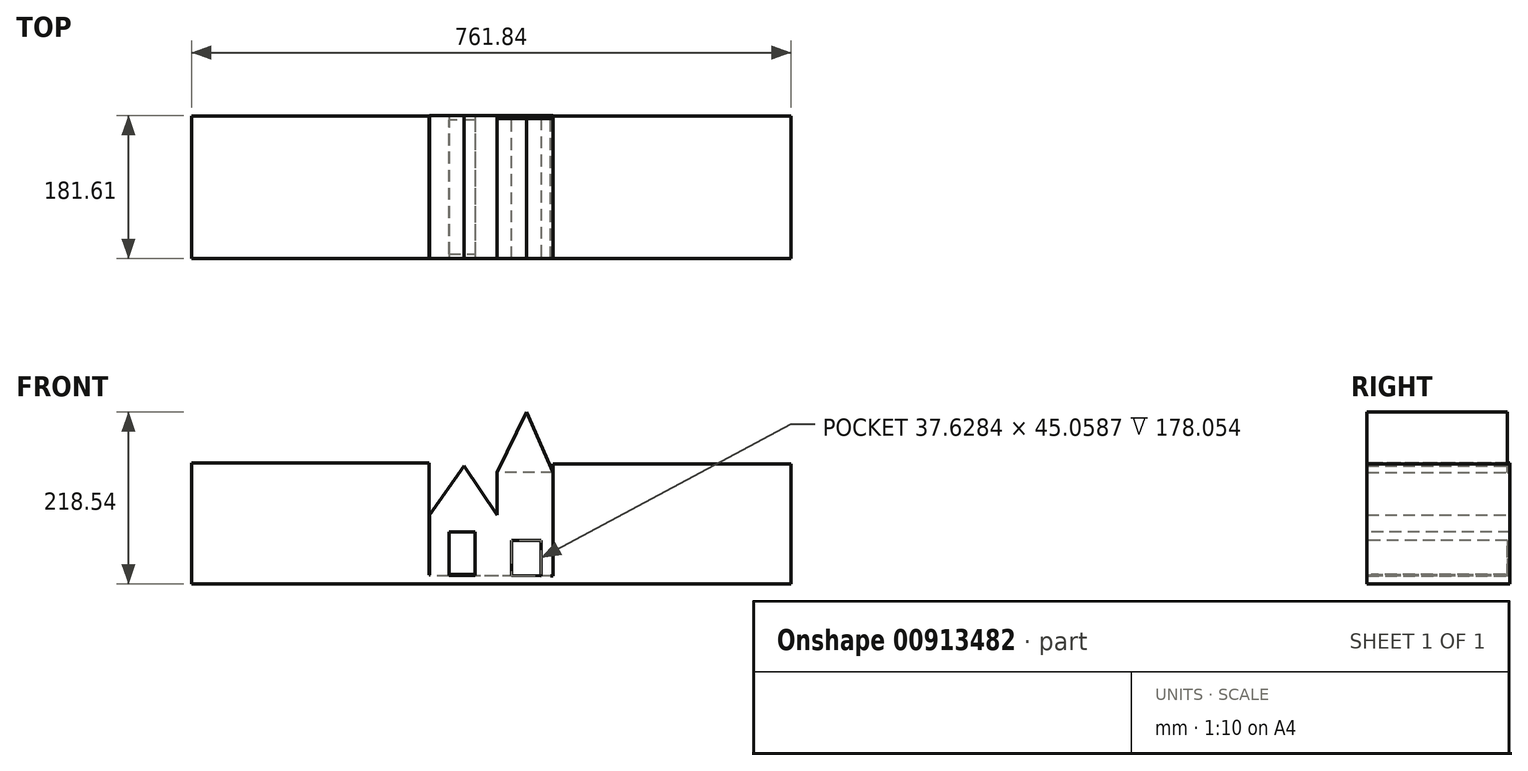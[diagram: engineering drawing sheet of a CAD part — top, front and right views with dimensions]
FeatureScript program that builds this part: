
annotation { "Feature Type Name" : "Feature", "Feature Type Description" : "" }
export const myFeature = defineFeature(function(context is Context, id is Id, definition is map)
    precondition{}
    {
        {
            var Q0;
            Q0=qCreatedBy(makeId("Front.planeOp"),FACE);
            var sketch = newSketch(context, id + "F0", { "sketchPlane" : qUnion([Q0])});
            skLineSegment(sketch, "E0", {"start": v(42.3, -77.57) * mm, "end": v(42.3, 0) * mm});
            skLineSegment(sketch, "E1", {"start": v(42.3, 0) * mm, "end": v(0, 62.2) * mm});
            skLineSegment(sketch, "E2", {"start": v(42.3, -77.57) * mm, "end": v(-43.65, -77.57) * mm});
            skLineSegment(sketch, "E3", {"start": v(0, 62.2) * mm, "end": v(-43.65, 0) * mm});
            skLineSegment(sketch, "E4", {"start": v(-43.65, 0) * mm, "end": v(-43.65, -77.57) * mm});
            skSolve(sketch);
        }
        {
            var Q0;
            Q0=makeQuery(id+"F0.imprint","IMPRINT",FACE,{"disambiguationData":[TD([[makeQuery(id+"F0.imprint","IMPRINT",EDGE,{"derivedFrom":sQuery(id+"F0.wireOp",EDGE,"E0")}),1.0]])]});
            extrude(context, id + "F1", {"entities" : qUnion([Q0]), "depth" : 25.4 * mm, "offsetDistance" : 25.4 * mm});
        }
        {
            var Q0;
            Q0=makeQuery(id+"F1.opExtrude","CAP_FACE",FACE,{"disambiguationData":[OSD([sQuery(id+"F0.wireOp",EDGE,"E0"),sQuery(id+"F0.wireOp",EDGE,"E1"),sQuery(id+"F0.wireOp",EDGE,"E2"),sQuery(id+"F0.wireOp",EDGE,"E3"),sQuery(id+"F0.wireOp",EDGE,"E4")])],"isStart":false});
            extrude(context, id + "F2", {"entities" : qUnion([Q0]), "operationType" : NewBodyOperationType.ADD, "depth" : 105.4 * mm, "offsetDistance" : 25.4 * mm});
        }
        {
            var Q0;
            Q0=makeQuery(id+"F2.opExtrude","CAP_FACE",FACE,{"disambiguationData":[OSD([sQuery(id+"F0.wireOp",EDGE,"E0"),sQuery(id+"F0.wireOp",EDGE,"E1"),sQuery(id+"F0.wireOp",EDGE,"E2"),sQuery(id+"F0.wireOp",EDGE,"E3"),sQuery(id+"F0.wireOp",EDGE,"E4")])],"isStart":false});
            var sketch = newSketch(context, id + "F3", { "sketchPlane" : qUnion([Q0])});
            skSolve(sketch);
        }
        {
            var Q0;
            Q0=makeQuery(id+"F3.imprint","IMPRINT",FACE,{"disambiguationData":[TD([[makeQuery(id+"F3.imprint","IMPRINT",EDGE,{"derivedFrom":makeQuery(id+"F2.opExtrude","CAP_EDGE",EDGE,{"disambiguationData":[OSD([sQuery(id+"F0.wireOp",EDGE,"E0")])],"isStart":false})}),1.0]])]});
            extrude(context, id + "F4", {"entities" : qUnion([Q0]), "operationType" : NewBodyOperationType.ADD, "depth" : 25.4 * mm, "offsetDistance" : 25.4 * mm});
        }
        {
            var Q0;
            Q0=makeQuery(id+"F4.opExtrude","CAP_FACE",FACE,{"disambiguationData":[OSD([sQuery(id+"F0.wireOp",EDGE,"E0"),sQuery(id+"F0.wireOp",EDGE,"E1"),sQuery(id+"F0.wireOp",EDGE,"E2"),sQuery(id+"F0.wireOp",EDGE,"E3"),sQuery(id+"F0.wireOp",EDGE,"E4")])],"isStart":false});
            var sketch = newSketch(context, id + "F5", { "sketchPlane" : qUnion([Q0])});
            skLineSegment(sketch, "E5", {"start": v(13.7, -77.57) * mm, "end": v(13.7, -34.13) * mm});
            skLineSegment(sketch, "E6", {"start": v(13.7, -77.57) * mm, "end": v(-17.83, -77.57) * mm});
            skLineSegment(sketch, "E7", {"start": v(-17.83, -78.03) * mm, "end": v(-17.83, -37.08) * mm});
            skLineSegment(sketch, "E8", {"start": v(-16.65, -37.08) * mm, "end": v(13.7, -37.08) * mm});
            skSolve(sketch);
        }
        {
            var Q0;
            {var subQ1=sQuery(id+"F5.wireOp",EDGE,"E6");Q0=makeQuery(id+"F5.imprint","IMPRINT",FACE,{"disambiguationData":[TD([[makeQuery(id+"F5.imprint","IMPRINT",EDGE,{"derivedFrom":subQ1}),-1.0]])]});}
            var sketch = newSketch(context, id + "F6", { "sketchPlane" : qUnion([Q0])});
            skLineSegment(sketch, "E9", {"start": v(-16.94, -78.91) * mm, "end": v(-16.94, -35.6) * mm});
            skLineSegment(sketch, "E10", {"start": v(-19.3, -35.6) * mm, "end": v(14, -35.6) * mm});
            skLineSegment(sketch, "E11", {"start": v(14, -35.01) * mm, "end": v(14, -78.33) * mm});
            skLineSegment(sketch, "E12", {"start": v(14, -78.33) * mm, "end": v(-16.94, -78.91) * mm});
            skSolve(sketch);
        }
        {
            var Q0;
            {var subQ1=sQuery(id+"F6.wireOp",EDGE,"E10");var subQ9=sQuery(id+"F6.wireOp",EDGE,"E9");var subQ11=makeQuery(id+"F6.imprint","INTERSECT",VERTEX,{"derivedFrom":[subQ9,subQ1]});Q0=makeQuery(id+"F6.imprint","IMPRINT",FACE,{"disambiguationData":[TD([[makeQuery(id+"F6.imprint","IMPRINT",EDGE,{"disambiguationData":[TD([[subQ11,1.0]])],"derivedFrom":subQ9}),-1.0]])]});}
            extrude(context, id + "F7", {"entities" : qUnion([Q0]), "operationType" : NewBodyOperationType.ADD, "oppositeDirection" : true, "depth" : 34.54 * mm, "offsetDistance" : 25.4 * mm});
        }
        {
            var Q0;
            {var subQ1=sQuery(id+"F5.wireOp",EDGE,"E6");Q0=makeQuery(id+"F5.imprint","IMPRINT",FACE,{"disambiguationData":[TD([[makeQuery(id+"F5.imprint","IMPRINT",EDGE,{"derivedFrom":subQ1}),-1.0]])]});}
            extrude(context, id + "F8", {"entities" : qUnion([Q0]), "operationType" : NewBodyOperationType.ADD, "depth" : 25.4 * mm, "offsetDistance" : 25.4 * mm});
        }
        {
            var Q0;
            Q0=makeQuery(id+"F8.opExtrude","CAP_FACE",FACE,{"disambiguationData":[OSD([sQuery(id+"F0.wireOp",EDGE,"E0"),sQuery(id+"F0.wireOp",EDGE,"E1"),sQuery(id+"F0.wireOp",EDGE,"E2"),sQuery(id+"F0.wireOp",EDGE,"E3"),sQuery(id+"F0.wireOp",EDGE,"E4"),sQuery(id+"F5.wireOp",EDGE,"E6")])],"isStart":false});
            var sketch = newSketch(context, id + "F9", { "sketchPlane" : qUnion([Q0])});
            skLineSegment(sketch, "E13", {"start": v(-19, -77.57) * mm, "end": v(-19, -22.05) * mm});
            skLineSegment(sketch, "E14", {"start": v(-19, -22.05) * mm, "end": v(14.3, -22.05) * mm});
            skLineSegment(sketch, "E15", {"start": v(14.3, -22.05) * mm, "end": v(14.3, -77.57) * mm});
            skLineSegment(sketch, "E16", {"start": v(14.3, -77.57) * mm, "end": v(-19, -77.57) * mm});
            skSolve(sketch);
        }
        {
            var Q0;
            Q0=makeQuery(id+"F9.imprint","IMPRINT",FACE,{"disambiguationData":[TD([[makeQuery(id+"F9.imprint","IMPRINT",EDGE,{"derivedFrom":sQuery(id+"F9.wireOp",EDGE,"E13")}),-1.0]])]});
            extrude(context, id + "F10", {"entities" : qUnion([Q0]), "operationType" : NewBodyOperationType.ADD, "depth" : 25.4 * mm, "offsetDistance" : 25.4 * mm});
        }
        {
            var Q0;
            Q0=makeQuery(id+"F10.opExtrude","CAP_FACE",FACE,{"disambiguationData":[OSD([sQuery(id+"F9.wireOp",EDGE,"E13"),sQuery(id+"F9.wireOp",EDGE,"E14"),sQuery(id+"F9.wireOp",EDGE,"E15"),sQuery(id+"F9.wireOp",EDGE,"E16")])],"isStart":false});
            extrude(context, id + "F11", {"entities" : qUnion([Q0]), "operationType" : NewBodyOperationType.REMOVE, "oppositeDirection" : true, "depth" : 249.68 * mm, "offsetDistance" : 25.4 * mm});
        }
        {
            var Q0;
            {var subQ0=sQuery(id+"F0.wireOp",EDGE,"E4");var subQ2=sQuery(id+"F0.wireOp",EDGE,"E2");var subQ5=sQuery(id+"F5.wireOp",EDGE,"E6");Q0=makeQuery(id+"F11.boolean.opBoolean","SPLIT",FACE,{"disambiguationData":[TD([makeQuery(id+"F1.opExtrude","SWEPT_FACE",FACE,{"disambiguationData":[OSD([subQ0])]})])],"derivedFrom":makeQuery(id+"F10.boolean.opBoolean","MERGE",FACE,{"derivedFrom":[makeQuery(id+"F8.boolean.opBoolean","MERGE",FACE,{"derivedFrom":[makeQuery(id+"F4.boolean.opBoolean","MERGE",FACE,{"derivedFrom":[makeQuery(id+"F2.boolean.opBoolean","MERGE",FACE,{"derivedFrom":[makeQuery(id+"F1.opExtrude","SWEPT_FACE",FACE,{"disambiguationData":[OSD([subQ2])]}),makeQuery(id+"F2.opExtrude","SWEPT_FACE",FACE,{"disambiguationData":[OSD([subQ2])]})]}),makeQuery(id+"F4.opExtrude","SWEPT_FACE",FACE,{"disambiguationData":[OSD([subQ2])]})]}),makeQuery(id+"F8.opExtrude","SWEPT_FACE",FACE,{"disambiguationData":[OSD([subQ2,subQ5])]})]}),makeQuery(id+"F10.opExtrude","SWEPT_FACE",FACE,{"disambiguationData":[OSD([sQuery(id+"F9.wireOp",EDGE,"E16")])]})]})});}
            var sketch = newSketch(context, id + "F12", { "sketchPlane" : qUnion([Q0])});
            skLineSegment(sketch, "E17", {"start": v(-38.28, 175.95) * mm, "end": v(-38.28, 6.02) * mm});
            skLineSegment(sketch, "E18", {"start": v(-38.28, 6.02) * mm, "end": v(34.83, 6.02) * mm});
            skLineSegment(sketch, "E19", {"start": v(34.83, 6.02) * mm, "end": v(34.83, 175.95) * mm});
            skLineSegment(sketch, "E20", {"start": v(34.83, 175.95) * mm, "end": v(-38.28, 175.95) * mm});
            skSolve(sketch);
        }
        {
            var Q0;
            {var subQ0=sQuery(id+"F12.wireOp",EDGE,"E19");Q0=makeQuery(id+"F12.imprint","IMPRINT",FACE,{"disambiguationData":[TD([[makeQuery(id+"F12.imprint","IMPRINT",EDGE,{"derivedFrom":subQ0}),1.0]])]});}
            var Q1;
            {var subQ0=sQuery(id+"F12.wireOp",EDGE,"E17");Q1=makeQuery(id+"F12.imprint","IMPRINT",FACE,{"disambiguationData":[TD([[makeQuery(id+"F12.imprint","IMPRINT",EDGE,{"derivedFrom":subQ0}),1.0]])]});}
            extrude(context, id + "F13", {"entities" : qUnion([Q0, Q1]), "operationType" : NewBodyOperationType.ADD, "oppositeDirection" : true, "depth" : 1.52 * mm, "offsetDistance" : 25.4 * mm});
        }
        {
            var Q0;
            {var subQ0=sQuery(id+"F0.wireOp",EDGE,"E0");Q0=makeQuery(id+"F8.boolean.opBoolean","MERGE",FACE,{"derivedFrom":[makeQuery(id+"F4.boolean.opBoolean","MERGE",FACE,{"derivedFrom":[makeQuery(id+"F2.boolean.opBoolean","MERGE",FACE,{"derivedFrom":[makeQuery(id+"F1.opExtrude","SWEPT_FACE",FACE,{"disambiguationData":[OSD([subQ0])]}),makeQuery(id+"F2.opExtrude","SWEPT_FACE",FACE,{"disambiguationData":[OSD([subQ0])]})]}),makeQuery(id+"F4.opExtrude","SWEPT_FACE",FACE,{"disambiguationData":[OSD([subQ0])]})]}),makeQuery(id+"F8.opExtrude","SWEPT_FACE",FACE,{"disambiguationData":[OSD([subQ0])]})]});}
            extrude(context, id + "F14", {"entities" : qUnion([Q0]), "operationType" : NewBodyOperationType.ADD, "depth" : 70.87 * mm, "offsetDistance" : 25.4 * mm});
        }
        {
            var Q0;
            {var subQ0=sQuery(id+"F0.wireOp",EDGE,"E0");Q0=makeQuery(id+"F14.boolean.opBoolean","MERGE",FACE,{"derivedFrom":[makeQuery(id+"F8.opExtrude","CAP_FACE",FACE,{"disambiguationData":[OSD([subQ0,sQuery(id+"F0.wireOp",EDGE,"E1"),sQuery(id+"F0.wireOp",EDGE,"E2"),sQuery(id+"F0.wireOp",EDGE,"E3"),sQuery(id+"F0.wireOp",EDGE,"E4"),sQuery(id+"F5.wireOp",EDGE,"E6")])],"isStart":false}),makeQuery(id+"F14.opExtrude","SWEPT_FACE",FACE,{"disambiguationData":[OSD([subQ0]),TDD([makeQuery(id+"F8.opExtrude","CAP_EDGE",EDGE,{"disambiguationData":[OSD([subQ0])],"isStart":false})])]})]});}
            var sketch = newSketch(context, id + "F15", { "sketchPlane" : qUnion([Q0])});
            skLineSegment(sketch, "E21", {"start": v(42.3, 0) * mm, "end": v(42.3, -77.57) * mm});
            skSolve(sketch);
        }
        {
            var Q0;
            {var subQ0=sQuery(id+"F15.wireOp",EDGE,"E21");Q0=makeQuery(id+"F15.imprint","IMPRINT",FACE,{"disambiguationData":[TD([[makeQuery(id+"F15.imprint","IMPRINT",EDGE,{"derivedFrom":subQ0}),1.0]])]});}
            var sketch = newSketch(context, id + "F16", { "sketchPlane" : qUnion([Q0])});
            skLineSegment(sketch, "E22", {"start": v(60.66, -77.54) * mm, "end": v(60.66, -32.45) * mm});
            skLineSegment(sketch, "E23", {"start": v(60.66, -32.45) * mm, "end": v(98.29, -32.45) * mm});
            skLineSegment(sketch, "E24", {"start": v(98.29, -32.45) * mm, "end": v(98.29, -77.54) * mm});
            skLineSegment(sketch, "E25", {"start": v(98.29, -77.54) * mm, "end": v(60.66, -77.54) * mm});
            skSolve(sketch);
        }
        {
            var Q0;
            Q0=makeQuery(id+"F16.imprint","IMPRINT",FACE,{"disambiguationData":[TD([[makeQuery(id+"F16.imprint","IMPRINT",EDGE,{"derivedFrom":sQuery(id+"F16.wireOp",EDGE,"E22")}),-1.0]])]});
            extrude(context, id + "F17", {"entities" : qUnion([Q0]), "operationType" : NewBodyOperationType.REMOVE, "oppositeDirection" : true, "depth" : 178.05 * mm, "offsetDistance" : 25.4 * mm});
        }
        {
            var Q0;
            Q0=makeQuery(id+"F14.opExtrude","SWEPT_FACE",FACE,{"disambiguationData":[OSD([sQuery(id+"F0.wireOp",EDGE,"E0"),sQuery(id+"F0.wireOp",EDGE,"E1")])]});
            extrude(context, id + "F18", {"entities" : qUnion([Q0]), "operationType" : NewBodyOperationType.ADD, "depth" : 53.6 * mm, "offsetDistance" : 25.4 * mm});
        }
        {
            var Q0;
            {var subQ0=sQuery(id+"F0.wireOp",EDGE,"E1");var subQ1=sQuery(id+"F0.wireOp",EDGE,"E0");Q0=makeQuery(id+"F18.boolean.opBoolean","MERGE",FACE,{"derivedFrom":[makeQuery(id+"F14.boolean.opBoolean","MERGE",FACE,{"derivedFrom":[makeQuery(id+"F8.opExtrude","CAP_FACE",FACE,{"disambiguationData":[OSD([subQ1,subQ0,sQuery(id+"F0.wireOp",EDGE,"E2"),sQuery(id+"F0.wireOp",EDGE,"E3"),sQuery(id+"F0.wireOp",EDGE,"E4"),sQuery(id+"F5.wireOp",EDGE,"E6")])],"isStart":false}),makeQuery(id+"F14.opExtrude","SWEPT_FACE",FACE,{"disambiguationData":[OSD([subQ1]),TDD([makeQuery(id+"F8.opExtrude","CAP_EDGE",EDGE,{"disambiguationData":[OSD([subQ1])],"isStart":false})])]})]}),makeQuery(id+"F18.opExtrude","SWEPT_FACE",FACE,{"disambiguationData":[OSD([subQ1,subQ0]),TDD([makeQuery(id+"F14.opExtrude","SWEPT_EDGE",EDGE,{"disambiguationData":[OSD([subQ1,subQ0]),TDD([makeQuery(id+"F8.opExtrude","CAP_VERTEX",VERTEX,{"disambiguationData":[OSD([subQ1,subQ0])],"isStart":false})])]})])]})]});}
            var sketch = newSketch(context, id + "F19", { "sketchPlane" : qUnion([Q0])});
            skLineSegment(sketch, "E26", {"start": v(42.3, 53.6) * mm, "end": v(79.4, 130.57) * mm});
            skLineSegment(sketch, "E27", {"start": v(79.4, 130.57) * mm, "end": v(113.16, 53.6) * mm});
            skSolve(sketch);
        }
        {
            var Q0;
            Q0=makeQuery(id+"F19.imprint","IMPRINT",FACE,{"disambiguationData":[TD([[makeQuery(id+"F19.imprint","IMPRINT",EDGE,{"derivedFrom":sQuery(id+"F19.wireOp",EDGE,"E26")}),-1.0]])]});
            extrude(context, id + "F20", {"entities" : qUnion([Q0]), "operationType" : NewBodyOperationType.ADD, "oppositeDirection" : true, "depth" : 178.05 * mm, "offsetDistance" : 25.4 * mm});
        }
        {
            var Q0;
            {var subQ3=sQuery(id+"F15.wireOp",EDGE,"E21");Q0=makeQuery(id+"F15.imprint","IMPRINT",FACE,{"disambiguationData":[TD([[makeQuery(id+"F15.imprint","IMPRINT",EDGE,{"derivedFrom":subQ3}),-1.0]])]});}
            var sketch = newSketch(context, id + "F21", { "sketchPlane" : qUnion([Q0])});
            skLineSegment(sketch, "E28", {"start": v(-43.82, -76.76) * mm, "end": v(-43.82, -87.97) * mm});
            skLineSegment(sketch, "E29", {"start": v(113.5, -77.6) * mm, "end": v(113.5, -87.97) * mm});
            skLineSegment(sketch, "E30", {"start": v(113.5, -87.97) * mm, "end": v(-43.82, -87.97) * mm});
            skLineSegment(sketch, "E31", {"start": v(-43.82, -76.76) * mm, "end": v(113.5, -77.6) * mm});
            skSolve(sketch);
        }
        {
            var Q0;
            {var subQ26=sQuery(id+"F21.wireOp",EDGE,"E28");Q0=makeQuery(id+"F21.imprint","IMPRINT",FACE,{"disambiguationData":[TD([[makeQuery(id+"F21.imprint","IMPRINT",EDGE,{"derivedFrom":subQ26}),1.0]])]});}
            extrude(context, id + "F22", {"entities" : qUnion([Q0]), "operationType" : NewBodyOperationType.ADD, "oppositeDirection" : true, "depth" : 181.1 * mm, "offsetDistance" : 25.4 * mm});
        }
        {
            var Q0;
            Q0=makeQuery(id+"F22.opExtrude","SWEPT_FACE",FACE,{"disambiguationData":[OSD([sQuery(id+"F21.wireOp",EDGE,"E28")])]});
            extrude(context, id + "F23", {"entities" : qUnion([Q0]), "operationType" : NewBodyOperationType.ADD, "depth" : 302.26 * mm, "offsetDistance" : 25.4 * mm});
        }
        {
            var Q0;
            Q0=makeQuery(id+"F22.opExtrude","SWEPT_FACE",FACE,{"disambiguationData":[OSD([sQuery(id+"F21.wireOp",EDGE,"E29")])]});
            extrude(context, id + "F24", {"entities" : qUnion([Q0]), "operationType" : NewBodyOperationType.ADD, "depth" : 302.26 * mm, "offsetDistance" : 25.4 * mm});
        }
        {
            var Q0;
            Q0=makeQuery(id+"F23.opExtrude","SWEPT_FACE",FACE,{"disambiguationData":[OSD([sQuery(id+"F21.wireOp",EDGE,"E28"),sQuery(id+"F21.wireOp",EDGE,"E31")])]});
            extrude(context, id + "F25", {"entities" : qUnion([Q0]), "operationType" : NewBodyOperationType.ADD, "depth" : 142.24 * mm, "offsetDistance" : 25.4 * mm});
        }
        {
            var Q0;
            Q0=makeQuery(id+"F24.opExtrude","SWEPT_FACE",FACE,{"disambiguationData":[OSD([sQuery(id+"F21.wireOp",EDGE,"E29"),sQuery(id+"F21.wireOp",EDGE,"E31")])]});
            extrude(context, id + "F26", {"entities" : qUnion([Q0]), "operationType" : NewBodyOperationType.ADD, "depth" : 142.24 * mm, "offsetDistance" : 25.4 * mm});
        }
    });
